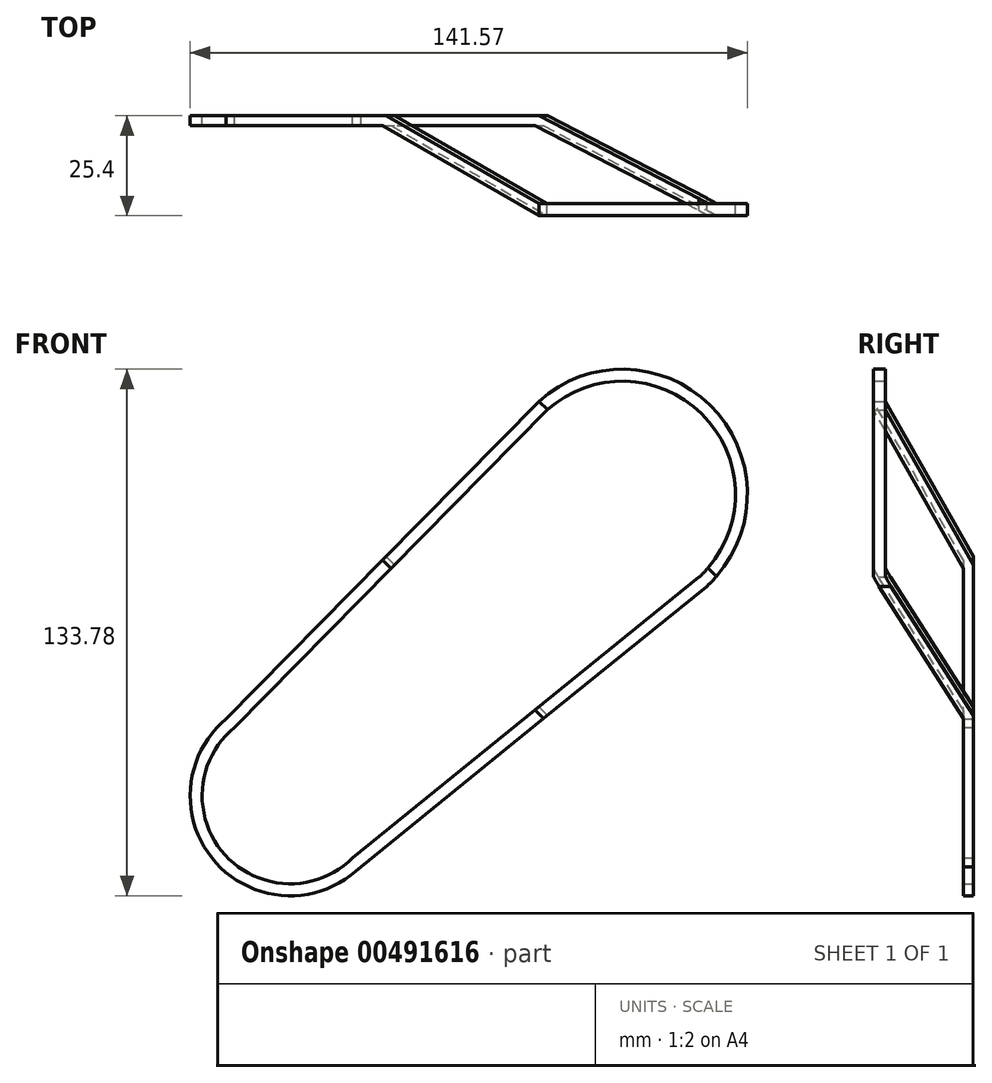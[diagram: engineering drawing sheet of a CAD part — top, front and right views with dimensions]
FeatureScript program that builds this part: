
annotation { "Feature Type Name" : "Feature", "Feature Type Description" : "" }
export const myFeature = defineFeature(function(context is Context, id is Id, definition is map)
    precondition{}
    {
        {
            var Q0;
            Q0=qCreatedBy(makeId("Front.planeOp"),FACE);
            var sketch = newSketch(context, id + "F0", { "sketchPlane" : qUnion([Q0])});
            skPoint(sketch, "E0.visualSharp", {"position": v(-70.83, -28.34) * mm});
            skPoint(sketch, "E1.visualSharp", {"position": v(-30.28, -68.28) * mm});
            skPoint(sketch, "E2.visualSharp", {"position": v(67.86, 31.35) * mm});
            skPoint(sketch, "E3.visualSharp", {"position": v(27.31, 71.3) * mm});
            skArc(sketch, "E4.1", {"start": v(-24.61, -58.08) * mm, "mid": v(-61.36, -57.15) * mm, "end": v(-58.78, -20.48) * mm});
            skArc(sketch, "E4.5", {"start": v(20.6, 60.15) * mm, "mid": v(65.34, 57.92) * mm, "end": v(63.3, 13.16) * mm});
            skLineSegment(sketch, "E5", {"start": v(-58.78, -20.48) * mm, "end": v(20.6, 60.15) * mm});
            skLineSegment(sketch, "E6", {"start": v(-24.61, -58.08) * mm, "end": v(63.3, 13.16) * mm});
            skLineSegment(sketch, "E7.0", {"start": v(-56.72, -22.74) * mm, "end": v(22.7, 57.95) * mm});
            skArc(sketch, "E7.1", {"start": v(-26.66, -55.8) * mm, "mid": v(-59.1, -55.1) * mm, "end": v(-56.72, -22.74) * mm});
            skLineSegment(sketch, "E7.2", {"start": v(-26.66, -55.8) * mm, "end": v(61.32, 15.47) * mm});
            skArc(sketch, "E7.3", {"start": v(22.7, 57.95) * mm, "mid": v(63.08, 55.87) * mm, "end": v(61.32, 15.47) * mm});
            skLineSegment(sketch, "E8.bottom", {"start": v(-42.54, -22.02) * mm, "end": v(-48, -22.02) * mm});
            skLineSegment(sketch, "E8.top", {"start": v(-42.54, -55.26) * mm, "end": v(-48, -55.26) * mm});
            skLineSegment(sketch, "E8.left", {"start": v(-42.54, -22.02) * mm, "end": v(-42.54, -55.26) * mm});
            skLineSegment(sketch, "E8.right", {"start": v(-48, -22.02) * mm, "end": v(-48, -55.26) * mm});
            skLineSegment(sketch, "E9", {"start": v(-19.1, 19.83) * mm, "end": v(21.83, -20.45) * mm});
            skSolve(sketch);
        }
        {
            var Q0;
            {var subQ5=sQuery(id+"F0.wireOp",EDGE,"E4.1");Q0=makeQuery(id+"F0.imprint","IMPRINT",FACE,{"disambiguationData":[TD([[makeQuery(id+"F0.imprint","IMPRINT",EDGE,{"derivedFrom":subQ5}),-1.0]])]});}
            var Q1;
            {var subQ1=sQuery(id+"F0.wireOp",EDGE,"E7.1");Q1=makeQuery(id+"F0.imprint","IMPRINT",FACE,{"disambiguationData":[TD([[makeQuery(id+"F0.imprint","IMPRINT",EDGE,{"derivedFrom":subQ1}),-1.0]])]});}
            extrude(context, id + "F1", {"entities" : qUnion([Q0, Q1]), "depth" : 2.54 * mm});
        }
        {
            var Q0;
            {var subQ8=sQuery(id+"F0.wireOp",EDGE,"E4.5");Q0=makeQuery(id+"F0.imprint","IMPRINT",FACE,{"disambiguationData":[TD([[makeQuery(id+"F0.imprint","IMPRINT",EDGE,{"derivedFrom":subQ8}),-1.0]])]});}
            var Q1;
            {var subQ0=sQuery(id+"F0.wireOp",EDGE,"E7.3");Q1=makeQuery(id+"F0.imprint","IMPRINT",FACE,{"disambiguationData":[TD([[makeQuery(id+"F0.imprint","IMPRINT",EDGE,{"derivedFrom":subQ0}),-1.0]])]});}
            extrude(context, id + "F2", {"entities" : qUnion([Q0, Q1]), "operationType" : NewBodyOperationType.ADD, "depth" : 25.4 * mm});
        }
        {
            var Q0;
            {var subQ0=sQuery(id+"F0.wireOp",EDGE,"E5");Q0=makeQuery(id+"F2.boolean.opBoolean","MERGE",FACE,{"derivedFrom":[makeQuery(id+"F1.opExtrude","SWEPT_FACE",FACE,{"disambiguationData":[OSD([subQ0])]}),makeQuery(id+"F2.opExtrude","SWEPT_FACE",FACE,{"disambiguationData":[OSD([subQ0])]})]});}
            var sketch = newSketch(context, id + "F3", { "sketchPlane" : qUnion([Q0])});
            skLineSegment(sketch, "E10", {"start": v(2.54, 0.74) * mm, "end": v(25.4, 57.32) * mm});
            skLineSegment(sketch, "E11", {"start": v(25.4, 57.32) * mm, "end": v(22.35, 57.32) * mm});
            skLineSegment(sketch, "E12", {"start": v(22.35, 57.32) * mm, "end": v(0, 2) * mm});
            skLineSegment(sketch, "E13.0", {"start": v(22.35, 87.16) * mm, "end": v(22.35, 53.8) * mm});
            skSolve(sketch);
        }
        {
            var Q0;
            Q0=makeQuery(id+"F3.imprint","IMPRINT",FACE,{"disambiguationData":[TD([[makeQuery(id+"F3.imprint","IMPRINT",EDGE,{"derivedFrom":sQuery(id+"F3.wireOp",EDGE,"E10")}),-1.0]])]});
            extrude(context, id + "F4", {"entities" : qUnion([Q0]), "operationType" : NewBodyOperationType.REMOVE, "endBound" : BoundingType.THROUGH_ALL, "oppositeDirection" : true, "depth" : 25.4 * mm});
        }
        {
            var Q0;
            {var subQ0=sQuery(id+"F3.wireOp",EDGE,"E12");Q0=makeQuery(id+"F3.imprint","IMPRINT",FACE,{"disambiguationData":[TD([[makeQuery(id+"F3.imprint","IMPRINT",EDGE,{"derivedFrom":subQ0}),-1.0]])]});}
            extrude(context, id + "F5", {"entities" : qUnion([Q0]), "operationType" : NewBodyOperationType.REMOVE, "endBound" : BoundingType.THROUGH_ALL, "oppositeDirection" : true, "depth" : 25.4 * mm});
        }
        {
            var Q0;
            {var subQ0=sQuery(id+"F0.wireOp",EDGE,"E5");Q0=makeQuery(id+"F2.boolean.opBoolean","MERGE",FACE,{"derivedFrom":[makeQuery(id+"F1.opExtrude","SWEPT_FACE",FACE,{"disambiguationData":[OSD([subQ0])]}),makeQuery(id+"F2.opExtrude","SWEPT_FACE",FACE,{"disambiguationData":[OSD([subQ0])]})]});}
            var sketch = newSketch(context, id + "F6", { "sketchPlane" : qUnion([Q0])});
            skLineSegment(sketch, "E14.bottom", {"start": v(22.35, 57.32) * mm, "end": v(0, 57.32) * mm});
            skLineSegment(sketch, "E14.top", {"start": v(22.35, 106.48) * mm, "end": v(0, 106.48) * mm});
            skLineSegment(sketch, "E14.left", {"start": v(22.35, 57.32) * mm, "end": v(22.35, 106.48) * mm});
            skLineSegment(sketch, "E14.right", {"start": v(0, 57.32) * mm, "end": v(0, 106.48) * mm});
            skSolve(sketch);
        }
        {
            var Q0;
            Q0 = qSketchRegion(id + "F6", true);
            extrude(context, id + "F7", {"entities" : qUnion([Q0]), "operationType" : NewBodyOperationType.REMOVE, "endBound" : BoundingType.THROUGH_ALL, "oppositeDirection" : true, "depth" : 25.4 * mm});
        }
    });
